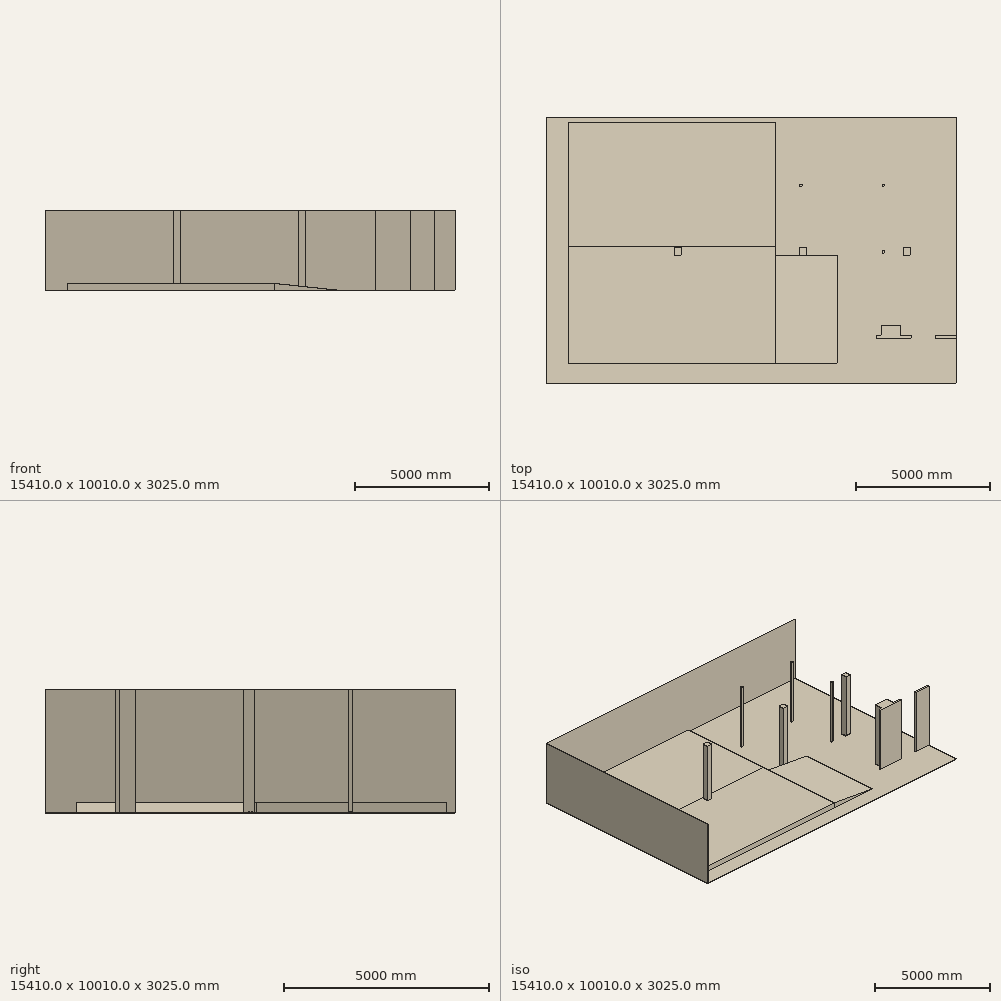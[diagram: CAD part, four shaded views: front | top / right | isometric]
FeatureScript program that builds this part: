
annotation { "Feature Type Name" : "Feature", "Feature Type Description" : "" }
export const myFeature = defineFeature(function(context is Context, id is Id, definition is map)
    precondition{}
    {
        {
            var Q0;
            Q0=qCreatedBy(makeId("Top.planeOp"),FACE);
            var sketch = newSketch(context, id + "F0", { "sketchPlane" : qUnion([Q0])});
            skLineSegment(sketch, "E0.bottom", {"start": v(4800, -4900) * mm, "end": v(5070, -4900) * mm});
            skLineSegment(sketch, "E0.top", {"start": v(4800, -5170) * mm, "end": v(5070, -5170) * mm});
            skLineSegment(sketch, "E0.left", {"start": v(4800, -4900) * mm, "end": v(4800, -5170) * mm});
            skLineSegment(sketch, "E0.right", {"start": v(5070, -4900) * mm, "end": v(5070, -5170) * mm});
            skLineSegment(sketch, "E1.bottom", {"start": v(9500, -4900) * mm, "end": v(9770, -4900) * mm});
            skLineSegment(sketch, "E1.top", {"start": v(9500, -5170) * mm, "end": v(9770, -5170) * mm});
            skLineSegment(sketch, "E1.left", {"start": v(9500, -4900) * mm, "end": v(9500, -5170) * mm});
            skLineSegment(sketch, "E1.right", {"start": v(9770, -4900) * mm, "end": v(9770, -5170) * mm});
            skLineSegment(sketch, "E2.bottom", {"start": v(13400, -5170) * mm, "end": v(13670, -5170) * mm});
            skLineSegment(sketch, "E2.top", {"start": v(13400, -4900) * mm, "end": v(13670, -4900) * mm});
            skLineSegment(sketch, "E2.left", {"start": v(13400, -5170) * mm, "end": v(13400, -4900) * mm});
            skLineSegment(sketch, "E2.right", {"start": v(13670, -5170) * mm, "end": v(13670, -4900) * mm});
            skLineSegment(sketch, "E3.bottom", {"start": v(9500, -2500) * mm, "end": v(9600, -2500) * mm});
            skLineSegment(sketch, "E3.top", {"start": v(9500, -2600) * mm, "end": v(9600, -2600) * mm});
            skLineSegment(sketch, "E3.left", {"start": v(9500, -2500) * mm, "end": v(9500, -2600) * mm});
            skLineSegment(sketch, "E3.right", {"start": v(9600, -2500) * mm, "end": v(9600, -2600) * mm});
            skLineSegment(sketch, "E4.bottom", {"start": v(12600, -2600) * mm, "end": v(12700, -2600) * mm});
            skLineSegment(sketch, "E4.top", {"start": v(12600, -2500) * mm, "end": v(12700, -2500) * mm});
            skLineSegment(sketch, "E4.left", {"start": v(12600, -2600) * mm, "end": v(12600, -2500) * mm});
            skLineSegment(sketch, "E4.right", {"start": v(12700, -2600) * mm, "end": v(12700, -2500) * mm});
            skLineSegment(sketch, "E5.bottom", {"start": v(12600, -5000) * mm, "end": v(12700, -5000) * mm});
            skLineSegment(sketch, "E5.top", {"start": v(12600, -5100) * mm, "end": v(12700, -5100) * mm});
            skLineSegment(sketch, "E5.left", {"start": v(12600, -5000) * mm, "end": v(12600, -5100) * mm});
            skLineSegment(sketch, "E5.right", {"start": v(12700, -5000) * mm, "end": v(12700, -5100) * mm});
            skSolve(sketch);
        }
        {
            var Q0;
            Q0 = qSketchRegion(id + "F0", true);
            extrude(context, id + "F1", {"entities" : qUnion([Q0]), "depth" : 3000 * mm});
        }
        {
            var Q0;
            Q0=qCreatedBy(makeId("Top.planeOp"),FACE);
            var sketch = newSketch(context, id + "F2", { "sketchPlane" : qUnion([Q0])});
            skLineSegment(sketch, "E6.bottom", {"start": v(0, 0) * mm, "end": v(15400, 0) * mm});
            skLineSegment(sketch, "E6.top", {"start": v(0, -10000) * mm, "end": v(15400, -10000) * mm});
            skLineSegment(sketch, "E6.left", {"start": v(0, 0) * mm, "end": v(0, -10000) * mm});
            skLineSegment(sketch, "E6.right", {"start": v(15400, 0) * mm, "end": v(15400, -10000) * mm});
            skSolve(sketch);
        }
        {
            var Q0;
            Q0 = qSketchRegion(id + "F2", true);
            extrude(context, id + "F3", {"entities" : qUnion([Q0]), "oppositeDirection" : true, "depth" : 25 * mm});
        }
        {
            var Q0;
            Q0=qCreatedBy(makeId("Right.planeOp"),FACE);
            var sketch = newSketch(context, id + "F4", { "sketchPlane" : qUnion([Q0])});
            skLineSegment(sketch, "E7.bottom", {"start": v(0, 0) * mm, "end": v(-10000, 0) * mm});
            skLineSegment(sketch, "E7.top", {"start": v(0, 3000) * mm, "end": v(-10000, 3000) * mm});
            skLineSegment(sketch, "E7.left", {"start": v(0, 0) * mm, "end": v(0, 3000) * mm});
            skLineSegment(sketch, "E7.right", {"start": v(-10000, 0) * mm, "end": v(-10000, 3000) * mm});
            skSolve(sketch);
        }
        {
            var Q0;
            Q0 = qSketchRegion(id + "F4", true);
            extrude(context, id + "F5", {"entities" : qUnion([Q0]), "operationType" : NewBodyOperationType.ADD, "oppositeDirection" : true, "depth" : 10 * mm, "offsetDistance" : 25 * mm});
        }
        {
            var Q0;
            Q0=qCreatedBy(makeId("Front.planeOp"),FACE);
            var sketch = newSketch(context, id + "F6", { "sketchPlane" : qUnion([Q0])});
            skLineSegment(sketch, "E8.bottom", {"start": v(0, 0) * mm, "end": v(15400, 0) * mm});
            skLineSegment(sketch, "E8.top", {"start": v(0, 3000) * mm, "end": v(15400, 3000) * mm});
            skLineSegment(sketch, "E8.left", {"start": v(0, 0) * mm, "end": v(0, 3000) * mm});
            skLineSegment(sketch, "E8.right", {"start": v(15400, 0) * mm, "end": v(15400, 3000) * mm});
            skSolve(sketch);
        }
        {
            var Q0;
            Q0 = qSketchRegion(id + "F6", true);
            extrude(context, id + "F7", {"entities" : qUnion([Q0]), "oppositeDirection" : true, "depth" : 10 * mm, "offsetDistance" : 25 * mm});
        }
        {
            var Q0;
            Q0 = qSketchRegion(id + "F0", true);
            extrude(context, id + "F8", {"entities" : qUnion([Q0]), "depth" : 25 * mm, "offsetDistance" : 25 * mm});
        }
        {
            var Q0;
            Q0=qCreatedBy(makeId("Top.planeOp"),FACE);
            var sketch = newSketch(context, id + "F9", { "sketchPlane" : qUnion([Q0])});
            skLineSegment(sketch, "E9.bottom", {"start": v(800, -200) * mm, "end": v(8600, -200) * mm});
            skLineSegment(sketch, "E9.top", {"start": v(800, -4850) * mm, "end": v(8600, -4850) * mm});
            skLineSegment(sketch, "E9.left", {"start": v(800, -200) * mm, "end": v(800, -4850) * mm});
            skLineSegment(sketch, "E9.right", {"start": v(8600, -200) * mm, "end": v(8600, -4850) * mm});
            skSolve(sketch);
        }
        {
            var Q0;
            Q0 = qSketchRegion(id + "F9", true);
            extrude(context, id + "F10", {"entities" : qUnion([Q0]), "depth" : 250 * mm, "offsetDistance" : 25 * mm});
        }
        {
            var Q0;
            Q0=qCreatedBy(makeId("Top.planeOp"),FACE);
            var sketch = newSketch(context, id + "F11", { "sketchPlane" : qUnion([Q0])});
            skLineSegment(sketch, "E10.bottom", {"start": v(800, -4850) * mm, "end": v(8600, -4850) * mm});
            skLineSegment(sketch, "E10.top", {"start": v(800, -9240) * mm, "end": v(8600, -9240) * mm});
            skLineSegment(sketch, "E10.left", {"start": v(800, -4850) * mm, "end": v(800, -9240) * mm});
            skLineSegment(sketch, "E10.right", {"start": v(8600, -4850) * mm, "end": v(8600, -9240) * mm});
            skSolve(sketch);
        }
        {
            var Q0;
            Q0 = qSketchRegion(id + "F11", true);
            extrude(context, id + "F12", {"entities" : qUnion([Q0]), "depth" : 250 * mm, "offsetDistance" : 25 * mm});
        }
        {
            var Q0;
            Q0=makeQuery(id+"F12.opExtrude","SWEPT_FACE",FACE,{"disambiguationData":[OSD([sQuery(id+"F11.wireOp",EDGE,"E10.top")])]});
            var sketch = newSketch(context, id + "F13", { "sketchPlane" : qUnion([Q0])});
            skLineSegment(sketch, "E11", {"start": v(8600, 0) * mm, "end": v(8600, 250) * mm});
            skLineSegment(sketch, "E12", {"start": v(8600, 250) * mm, "end": v(10936.66, 0) * mm});
            skLineSegment(sketch, "E13", {"start": v(10936.66, 0) * mm, "end": v(8600, 0) * mm});
            skSolve(sketch);
        }
        {
            var Q0;
            Q0 = qSketchRegion(id + "F13", true);
            var Q1;
            Q1=makeQuery(id+"F1.opExtrude","SWEPT_FACE",FACE,{"disambiguationData":[OSD([sQuery(id+"F0.wireOp",EDGE,"E1.top")])]});
            extrude(context, id + "F14", {"entities" : qUnion([Q0]), "endBound" : BoundingType.UP_TO_SURFACE, "oppositeDirection" : true, "depth" : 25 * mm, "endBoundEntityFace" : qUnion([Q1]), "offsetDistance" : 25 * mm});
        }
        {
            var Q0;
            Q0=makeQuery(id+"F3.opExtrude","CAP_FACE",FACE,{"disambiguationData":[OSD([sQuery(id+"F2.wireOp",EDGE,"E6.bottom"),sQuery(id+"F2.wireOp",EDGE,"E6.top"),sQuery(id+"F2.wireOp",EDGE,"E6.left"),sQuery(id+"F2.wireOp",EDGE,"E6.right")])],"isStart":true});
            var sketch = newSketch(context, id + "F15", { "sketchPlane" : qUnion([Q0])});
            skLineSegment(sketch, "E14", {"start": v(15400, -8300) * mm, "end": v(12400, -8300) * mm});
            skLineSegment(sketch, "E15", {"start": v(12400, -8300) * mm, "end": v(12400, -8200) * mm});
            skLineSegment(sketch, "E16", {"start": v(12400, -8200) * mm, "end": v(12574.73, -8200) * mm});
            skLineSegment(sketch, "E17", {"start": v(12574.73, -8200) * mm, "end": v(12574.73, -7800) * mm});
            skLineSegment(sketch, "E18", {"start": v(12574.73, -7800) * mm, "end": v(13279.13, -7800) * mm});
            skLineSegment(sketch, "E19", {"start": v(13279.13, -7800) * mm, "end": v(13279.13, -8200) * mm});
            skLineSegment(sketch, "E20", {"start": v(13279.13, -8200) * mm, "end": v(15400, -8200) * mm});
            skLineSegment(sketch, "E21", {"start": v(15400, -8200) * mm, "end": v(15400, -8300) * mm});
            skSolve(sketch);
        }
        {
            var Q0;
            Q0 = qSketchRegion(id + "F15", true);
            extrude(context, id + "F16", {"entities" : qUnion([Q0]), "depth" : 3000 * mm, "offsetDistance" : 25 * mm});
        }
        {
            var Q0;
            Q0=makeQuery(id+"F16.opExtrude","SWEPT_FACE",FACE,{"disambiguationData":[OSD([sQuery(id+"F15.wireOp",EDGE,"E14")])]});
            var sketch = newSketch(context, id + "F17", { "sketchPlane" : qUnion([Q0])});
            skLineSegment(sketch, "E22.bottom", {"start": v(14600, 0) * mm, "end": v(13700, 0) * mm});
            skLineSegment(sketch, "E22.top", {"start": v(14600, 3001) * mm, "end": v(13700, 3001) * mm});
            skLineSegment(sketch, "E22.left", {"start": v(14600, 0) * mm, "end": v(14600, 3001) * mm});
            skLineSegment(sketch, "E22.right", {"start": v(13700, 0) * mm, "end": v(13700, 3001) * mm});
            skSolve(sketch);
        }
        {
            var Q0;
            Q0 = qSketchRegion(id + "F17", true);
            extrude(context, id + "F18", {"entities" : qUnion([Q0]), "operationType" : NewBodyOperationType.REMOVE, "endBound" : BoundingType.UP_TO_NEXT, "oppositeDirection" : true, "depth" : 25 * mm, "offsetDistance" : 25 * mm});
        }
    });
